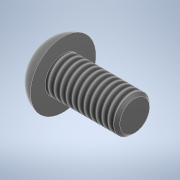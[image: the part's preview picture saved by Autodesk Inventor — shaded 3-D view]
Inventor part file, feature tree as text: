
AUTODESK INVENTOR PART (.ipt)
format: ipt  version: 2022 (Build 260153000, 153)  size: 142,336 bytes
history: native  units: mm
features: sketch x2, revolve x1, extrude x1, thread x1, chamfer x1
ambient origin geometry x8: Origin, YZ Plane, XZ Plane, XY Plane, X Axis, Y Axis, Z Axis, Center Point
bodies: Solid1 (feature_tree)
feature tree (6):
  revolve  "Revolution1"  [1 undecoded]
  extrude  "Extrusion1"  Depth=2.0mm
  thread  "Thread1"  [1 undecoded]
  chamfer  "Chamfer1"  Distance=2.0mm
  sketch  "Sketch1"  dims[d0=1.5mm d1=3.0mm]
  sketch  "Sketch2"  dims[d2=5.5mm d3=3.0mm d4=6.0mm d5=2.0mm d6=90.0deg d7=2.0mm d8=1.0mm d9=0.0mm d10=6.0mm d11=0.0mm d12=0.25mm d13=2.0mm d14=45.0deg]
note: 2 required parameter values undecoded (feature->parameter linkage not recoverable at this tier; creation-order binding heuristic only, values carry confidence <= 0.55)